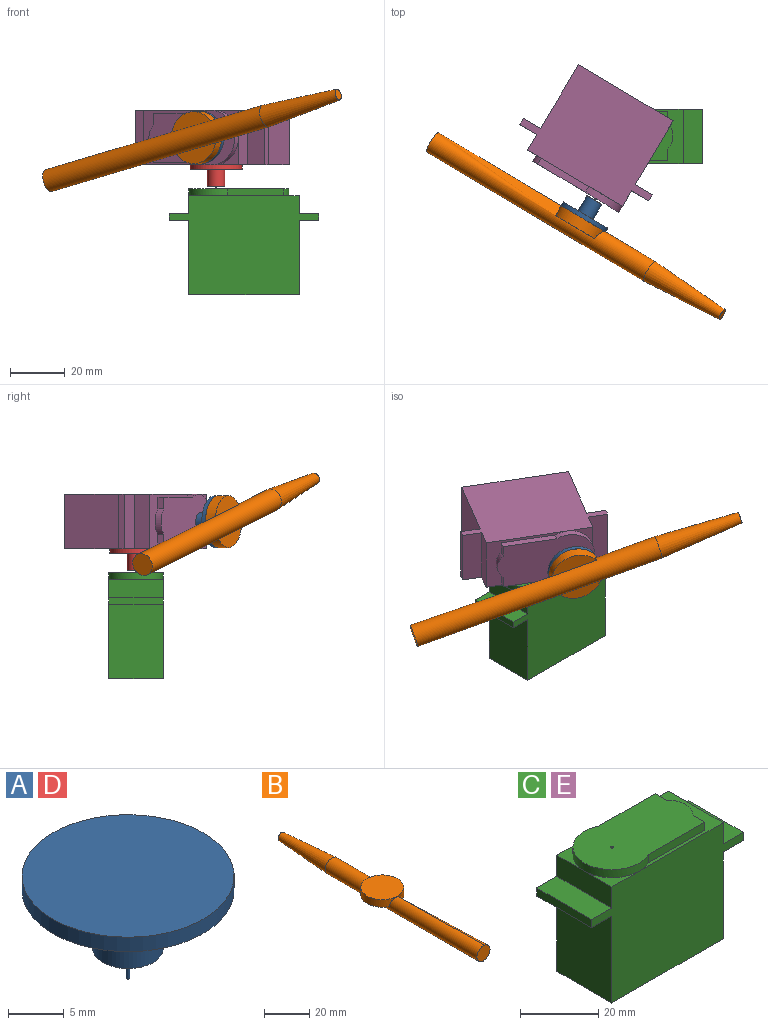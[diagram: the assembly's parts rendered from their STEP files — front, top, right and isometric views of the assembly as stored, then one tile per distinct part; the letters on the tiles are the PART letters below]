
ASSEMBLY  parts=5 mates=7
PART A: 7 faces, bbox 19.1x19.1x11.2 mm
  f0: cylinder r=0.16mm len=3.3mm, axis (0,0,1), area 3.3mm2, adj f1,f3
  f1: plane 0.32x0.32mm, normal (0,0,-1), area 0.1mm2, adj f0
  f2: cylinder r=3.17mm len=6.35mm, axis (0,0,-1), area 126.7mm2, adj f3,f6
  f3: plane 6.35x6.35mm, normal (0,0,-1), area 31.6mm2, adj f0,f2
  f4: cylinder r=9.53mm len=19.05mm, axis (0,0,-1), area 95mm2, adj f5,f6
  f5: plane 19.05x19.05mm, normal (0,0,1), area 285mm2, adj f4
  f6: plane 19.05x19.05mm, normal (0,0,-1), area 253.4mm2, adj f2,f4
PART B: 11 faces, bbox 19.1x127x8.3 mm
  f0: cylinder r=4.13mm len=95.25mm, axis (0,1,0), area 2247.6mm2, adj f1,f3,f4,f5,f6,f7,f8,f9
  f1: cylinder r=9.53mm len=0.04mm, axis (0,0,-1), area 0mm2, adj f0,f2
  f2: plane 19.05x19.05mm, normal (0,0,1), area 285mm2, adj f1,f4,f6,f8
  f3: plane 17.17x5.4mm, normal (0,0,-1), area 66.4mm2, adj f0,f4
  f4: cylinder r=9.53mm len=19.05mm, axis (0,0,-1), area 123.5mm2, adj f0,f2,f3
  f5: plane 8.26x8.26mm, normal (0,-1,0), area 53.5mm2, adj f0
  f6: cylinder r=9.53mm len=0.04mm, axis (0,0,-1), area 0mm2, adj f0,f2
  f7: plane 17.17x5.4mm, normal (0,0,-1), area 66.4mm2, adj f0,f8
  f8: cylinder r=9.53mm len=19.05mm, axis (0,0,-1), area 123.5mm2, adj f0,f2,f7
  f9: cone r=2.06mm half-angle=3.7deg, axis (0,-1,0), area 618.9mm2, adj f0,f10
  f10: plane 4.13x4.13mm, normal (0,1,0), area 13.4mm2, adj f9
PART C: 25 faces, bbox 54.7x19.9x38.9 mm
  f0: plane 30.33x19.86mm, normal (0,0,1), area 142.6mm2, adj f12,f14,f15,f16,f17,f18,f19,f20
  f1: plane 9.93x9.93mm, normal (0,0,1), area 21.2mm2, adj f2,f15,f16
  f2: plane 19.86x6.6mm, normal (-1,0,0), area 131.2mm2, adj f1,f3,f13,f14,f15
  f3: plane 19.86x7.24mm, normal (0,0,1), area 143.8mm2, adj f2,f4,f14,f15
  f4: plane 19.86x2.54mm, normal (-1,0,0), area 50.5mm2, adj f3,f5,f14,f15
  f5: plane 19.86x7.24mm, normal (0,0,-1), area 143.8mm2, adj f4,f6,f14,f15
  f6: plane 27.18x19.86mm, normal (-1,0,0), area 539.8mm2, adj f5,f7,f14,f15
  f7: plane 40.26x19.86mm, normal (0,0,-1), area 799.7mm2, adj f6,f8,f14,f15
  f8: plane 27.18x19.86mm, normal (1,0,0), area 539.8mm2, adj f7,f9,f14,f15
  f9: plane 19.86x7.24mm, normal (0,0,-1), area 143.8mm2, adj f8,f10,f14,f15
  f10: plane 19.86x2.54mm, normal (1,0,0), area 50.5mm2, adj f9,f11,f14,f15
  f11: plane 19.86x7.24mm, normal (0,0,1), area 143.8mm2, adj f10,f12,f14,f15
  f12: plane 19.86x6.6mm, normal (1,0,0), area 131.2mm2, adj f0,f11,f14,f15
  f13: plane 9.93x9.93mm, normal (0,0,1), area 21.2mm2, adj f2,f14,f16
  f14: plane 54.74x36.32mm, normal (0,-1,0), area 1499.1mm2, adj f0,f2,f3,f4,f5,f6,f7,f8
  f15: plane 54.74x36.32mm, normal (0,1,0), area 1499.1mm2, adj f0,f1,f2,f3,f4,f5,f6,f7
  f16: cylinder r=9.93mm len=19.86mm, axis (0,0,-1), area 101.8mm2, adj f0,f1,f13,f17,f21,f22
  f17: plane 20.32x2.54mm, normal (0,-1,0), area 51.6mm2, adj f0,f16,f18,f22
  f18: plane 4.19x2.54mm, normal (1,0,0), area 10.6mm2, adj f0,f17,f19,f22
  f19: cylinder r=6.6mm len=9.53mm, axis (0,0,-1), area 27mm2, adj f0,f18,f20,f22
  f20: plane 4.19x2.54mm, normal (1,0,0), area 10.6mm2, adj f0,f19,f21,f22
  f21: plane 20.31x2.54mm, normal (0,1,0), area 51.6mm2, adj f0,f16,f20,f22
  f22: plane 36.58x19.86mm, normal (0,0,1), area 614.2mm2, adj f16,f17,f18,f19,f20,f21,f23
  f23: cylinder r=0.41mm len=3.18mm, axis (0,0,1), area 8.2mm2, adj f22,f24
  f24: plane 0.83x0.83mm, normal (0,0,1), area 0.5mm2, adj f23
PART D: same geometry as A
PART E: same geometry as C
PLACE A rot(axis=(0.72,0.3,-0.63),129.9deg) t=(-12.27,-23.44,57.49)mm
PLACE B rot(axis=(-0.59,-0.44,-0.68),148.7deg) t=(-18.44,-33.81,57.49)mm
PLACE C t=(-20.13,9.93,36.32)mm
PLACE D rot(axis=(0,0,1),149.3deg) t=(-10.2,0,39.62)mm
PLACE E rot(axis=(-0.19,-0.69,0.69),158.4deg) t=(-2.05,-25.68,47.56)mm
MATE pin_slot C.f16 <-> D.f0  axis (0,0,-1) through (-10.2,0,36.32)mm
MATE cylindrical E.f16 <-> A.f0  axis (0.51,0.86,0) through (-10.59,-20.61,57.49)mm
MATE cylindrical C.f16 <-> D.f0  axis (0,0,-1) through (-10.2,0,36.32)mm
MATE fastened E.f15 <-> D.f4  axis (0,0,-1) through (-10.2,0,47.56)mm
MATE fastened B.f1 <-> A.f4  axis (0.51,0.86,0) through (-16.33,-30.27,57.49)mm
MATE pin_slot E.f16 <-> A.f0  axis (0.51,0.86,0) through (-10.59,-20.61,57.49)mm
MATE pin_slot C.f16 <-> D.f0  axis (0,0,-1) through (-10.2,0,36.32)mm
